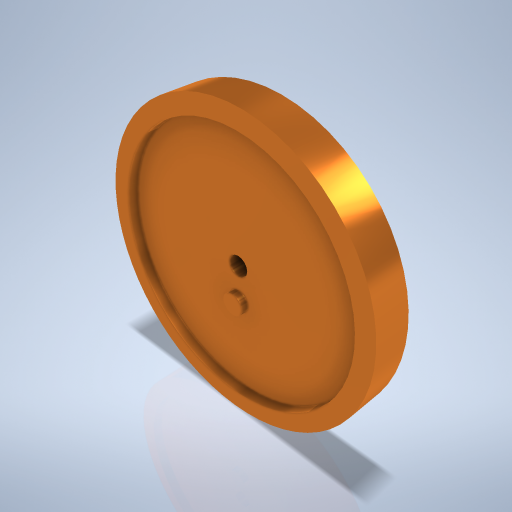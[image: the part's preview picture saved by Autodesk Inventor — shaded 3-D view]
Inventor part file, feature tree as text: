
AUTODESK INVENTOR PART (.ipt)
format: ipt  version: 2024.2 (Build 282272000, 272)  size: 284,672 bytes
history: native  units: mm
features: sketch x5, extrude x3, hole x2, mirror x1
ambient origin geometry x8: Origin, YZ Plane, XZ Plane, XY Plane, X Axis, Y Axis, Z Axis, Center Point
bodies: Volumenkörper1 (feature_tree)
feature tree (11):
  extrude  "Extrusion1"  Depth=50.0mm TaperAngle=0.0deg
  hole  "Bohrung1"  [1 undecoded]
  mirror  "Spiegeln1"
  extrude  "Extrusion2"  Depth=30.0mm
  hole  "Bohrung2"  [1 undecoded]
  extrude  "Extrusion3"  [1 undecoded]
  sketch  "Skizze1"  dims[d0=400.0mm d2=50.0mm d3=0.0mm]
  sketch  "Skizze2"  dims[d4=350.0mm d5=6.0mm d6=4.0mm d7=2.0mm d8=90.0deg d9=15.0mm d10=0.0mm d11=150.0mm]
  sketch  "Skizze3"  dims[d12=50.0mm d13=0.0mm]
  sketch  "Skizze4"  dims[d14=28.0mm d15=6.0mm d16=4.0mm d17=2.0mm d18=90.0deg d19=15.0mm d20=0.0mm d46=30.0mm]
  sketch  "Skizze7"  dims[d48=10.0mm d49=0.0mm d50=48.21mm]
note: 3 required parameter values undecoded (feature->parameter linkage not recoverable at this tier; creation-order binding heuristic only, values carry confidence <= 0.55)
